FCSTD DOCUMENT  (FreeCAD 1.1R40444 (Git))
Label: Assembly
License: All rights reserved
LicenseURL: http://en.wikipedia.org/wiki/All_rights_reserved
objects: App::Link×5, App::FeaturePython×4, App::Point×1, Assembly::JointGroup×1, Assembly::AssemblyObject×1
EXTERNAL_REF file=Hull.FCStd obj=Body
EXTERNAL_REF file=Hull.FCStd obj=Sketch
EXTERNAL_REF file=Hull.FCStd obj=Body001
EXTERNAL_REF file=Gears.FCStd obj=Body001
EXTERNAL_REF file=Gears.FCStd obj=Body

FEATURE [App::Link] Hull
  LinkPlacement = pos=(0,0,0) rot=(0,1,0;0.032426rad)
  LinkedObject = -> <external Hull.FCStd>#Body
  Placement = pos=(0,0,0) rot=(0,1,0;0.032426rad)
FEATURE [App::FeaturePython] GroundedJoint  # Assembly grounded joint (typed FeaturePython)
  ObjectToGround = -> Hull
FEATURE [App::Link] Sketch
  LinkPlacement = pos=(-25.4586,-4.64916e-06,39) rot=(0,0,1;0rad)
  LinkedObject = -> <external Hull.FCStd>#Sketch
  Placement = pos=(-25.4586,-4.64916e-06,39) rot=(0,0,1;0rad)
FEATURE [App::Point] Origin001  label="Origin"
  Role = Origin
FEATURE [App::Link] Lid
  LinkPlacement = pos=(0.818028,-8.2e-14,22.9856) rot=(0,1,0;0.032426rad)
  LinkedObject = -> <external Hull.FCStd>#Body001
  Placement = pos=(0.818028,-8.2e-14,22.9856) rot=(0,1,0;0.032426rad)
FEATURE [App::FeaturePython] Joint  label="Fixed002"  # Assembly joint (typed FeaturePython)
  Activated = true
  AngleMax = 0
  AngleMin = 0
  Detach1 = false
  Detach2 = false
  Distance = 0
  Distance2 = 0
  EnableAngleMax = false
  EnableAngleMin = false
  EnableLengthMax = false
  EnableLengthMin = false
  JointType = 0 (Fixed)
  LengthMax = 0
  LengthMin = 0
  Placement1 = pos=(12.6239,8.51e-14,-1) rot=(0,0,1;0rad)
  Placement2 = pos=(12.6963,1.1e-15,22) rot=(0,0,1;0rad)
  Reference1 = -> Assembly [Lid.Pocket.Face7,Lid.Pocket.Face7]
  Reference2 = -> Assembly [Hull.Thickness.Face6,Hull.Thickness.Face6]
FEATURE [App::Link] SecondaryGear
  LinkPlacement = pos=(25.5722,1.157e-13,1.17155) rot=(0,1,0;0.032426rad)
  LinkedObject = -> <external Gears.FCStd>#Body001
  Placement = pos=(25.5722,1.157e-13,1.17155) rot=(0,1,0;0.032426rad)
FEATURE [App::FeaturePython] Joint001  label="Revolute006"  # Assembly joint (typed FeaturePython)
  Activated = true
  AngleMax = 0
  AngleMin = 0
  Detach1 = false
  Detach2 = false
  Distance = 0
  Distance2 = 0
  EnableAngleMax = false
  EnableAngleMin = false
  EnableLengthMax = false
  EnableLengthMin = false
  JointType = 1 (Revolute)
  LengthMax = 0
  LengthMin = 0
  Placement2 = pos=(25.5208,0,2) rot=(0,0,1;0rad)
  Reference1 = -> Assembly [SecondaryGear.Sketch003.Edge1,SecondaryGear.Sketch003.Edge1]
  Reference2 = -> Assembly [Hull.Face11,Hull.Edge3]
FEATURE [App::Link] MainGear
  LinkPlacement = pos=(-25.4515,-0.0167118,2.82664) rot=(0,1,0;0.032426rad)
  LinkedObject = -> <external Gears.FCStd>#Body
  Placement = pos=(-25.4515,-0.0167118,2.82664) rot=(0,1,0;0.032426rad)
FEATURE [App::FeaturePython] Joint002  label="Revolute008"  # Assembly joint (typed FeaturePython)
  Activated = true
  AngleMax = 0
  AngleMin = 0
  Detach1 = false
  Detach2 = false
  Distance = 0
  Distance2 = 0
  EnableAngleMax = false
  EnableAngleMin = false
  EnableLengthMax = false
  EnableLengthMin = false
  JointType = 1 (Revolute)
  LengthMax = 0
  LengthMin = 0
  Placement1 = pos=(0.00903,0.01671,0) rot=(0,0,1;0rad)
  Placement2 = pos=(-25.5208,0,2) rot=(0,0,1;0rad)
  Reference1 = -> Assembly [MainGear.Face241,MainGear.Edge104]
  Reference2 = -> Assembly [Hull.Face11,Hull.Edge1]
FEATURE [Assembly::JointGroup] Joints
  Group = -> [GroundedJoint,Joint,Joint001,Joint002]
FEATURE [Assembly::AssemblyObject] Assembly
  Group = -> [Joints,Hull,GroundedJoint,Sketch,Lid,Joint,SecondaryGear,Joint001,MainGear,Joint002]
  Origin = -> Origin
  Type = Assembly

RESOLVED EXTERNAL PARTS (link-assembly join: the EXTERNAL_REF files above that resolve inside this repo's crawl, each included once):
---- part Gears.FCStd = doc fcstd_c6806c5b29c4 ----
FCSTD DOCUMENT  (FreeCAD 1.1R40444 (Git))
Label: Gears
License: All rights reserved
LicenseURL: http://en.wikipedia.org/wiki/All_rights_reserved
objects: PartDesign::Pad×4, Sketcher::SketchObject×4, PartDesign::Body×3, App::Point×3, Part::Part2DObjectPython×2, PartDesign::ShapeBinder×2, PartDesign::Pocket×1
note: 30 computed .brp shape members not serialized (recipe doc carries the construction recipe); baked Part::Feature solids carry a one-line shape summary decoded from their .brp
EXTERNAL_REF file=Configuration.FCStd obj=Spreadsheet

FEATURE [Part::Part2DObjectPython] InvoluteGear  # Draft 2D object (typed FeaturePython)
  AddendumCoefficient = 1
  DedendumCoefficient = 1.25
  ExternalGear = true
  HighPrecision = true
  Modules = 1
  NumberOfTeeth = 24
  PressureAngle = 20
  ProfileShiftCoefficient = 0
  RootFilletCoefficient = 0.38
  expr: Modules = Configuration#Spreadsheet.gear_module
  expr: NumberOfTeeth = Configuration#<<Spreadsheet>>.main_gear_teeth
FEATURE [Part::Part2DObjectPython] InvoluteGear002  # Draft 2D object (typed FeaturePython)
  AddendumCoefficient = 1
  DedendumCoefficient = 1.25
  ExternalGear = true
  HighPrecision = true
  Modules = 1
  NumberOfTeeth = 48
  PressureAngle = 20
  ProfileShiftCoefficient = 0
  RootFilletCoefficient = 0.38
  expr: Modules = Configuration#Spreadsheet.gear_module
  expr: NumberOfTeeth = Configuration#Spreadsheet.secondary_gear_teeth
FEATURE [PartDesign::Pad] Pad
  Direction = (0,0,1)
  Length = 20
  Length2 = 10
  Profile = -> InvoluteGear
  ReferenceAxis = -> InvoluteGear [N_Axis]
  Refine = true
  Suppressed = false
  Type = 0
  expr: Length = <<Configuration>>#<<Spreadsheet>>.gear_height
FEATURE [PartDesign::Body] Body  label="MainGear"
  AllowCompound = false
  Group = -> [InvoluteGear,Pad]
  Origin = -> Origin
  Tip = -> Pad
FEATURE [PartDesign::Pad] Pad001
  Direction = (0,0,1)
  Length = 20
  Length2 = 10
  Profile = -> InvoluteGear002
  ReferenceAxis = -> InvoluteGear002 [N_Axis]
  Refine = true
  Suppressed = false
  Type = 0
  expr: Length = Configuration#<<Spreadsheet>>.gear_height
FEATURE [Sketcher::SketchObject] Sketch  label="ShaftMountInterface"
  ArcFitTolerance = 0
  ExternalTypes = [0]
  FullyConstrained = true
  MakeInternals = false
  expr: Constraints[26] = 1
  sketch-geometry (13):
    g0: LineSegment StartX=-4 StartY=-5 StartZ=0 EndX=4 EndY=-5 EndZ=0
    g1: LineSegment StartX=5 StartY=-4 StartZ=0 EndX=5 EndY=4 EndZ=0
    g2: LineSegment StartX=4 StartY=5 StartZ=0 EndX=-4 EndY=5 EndZ=0
    g3: LineSegment StartX=-5 StartY=4 StartZ=0 EndX=-5 EndY=-4 EndZ=0
    g4: GeomPoint [constr] X=0 Y=0 Z=0
    g5: ArcOfCircle CenterX=-4 CenterY=4 CenterZ=0 NormalX=0 NormalY=0 NormalZ=1 AngleXU=0 Radius=1 StartAngle=1.5708 EndAngle=3.14159
    g6: GeomPoint [constr] X=-5 Y=5 Z=0
    g7: ArcOfCircle CenterX=4 CenterY=4 CenterZ=0 NormalX=0 NormalY=0 NormalZ=1 AngleXU=0 Radius=1 StartAngle=0 EndAngle=1.5708
    g8: GeomPoint [constr] X=5 Y=5 Z=0
    g9: ArcOfCircle CenterX=4 CenterY=-4 CenterZ=0 NormalX=0 NormalY=0 NormalZ=1 AngleXU=0 Radius=1 StartAngle=4.71239 EndAngle=6.28319
    g10: GeomPoint [constr] X=5 Y=-5 Z=0
    g11: ArcOfCircle CenterX=-4 CenterY=-4 CenterZ=0 NormalX=0 NormalY=0 NormalZ=1 AngleXU=0 Radius=1 StartAngle=3.14159 EndAngle=4.71239
    g12: GeomPoint [constr] X=-5 Y=-5 Z=0
  constraints (28):
    c: Horizontal(g0)
    c: Horizontal(g2)
    c: Vertical(g1)
    c: Vertical(g3)
    c: Symmetric(g8,g12,g4)
    c: Coincident(g4,g-1)
    c: PointOnObject(g6,g2)
    c: PointOnObject(g6,g3)
    c: Tangent(g2,g5) = -1.5708
    c: Tangent(g3,g5) = -1.5708
    c: PointOnObject(g8,g1)
    c: PointOnObject(g8,g2)
    c: Tangent(g1,g7) = -1.5708
    c: Tangent(g2,g7) = -1.5708
    c: PointOnObject(g10,g0)
    c: PointOnObject(g10,g1)
    c: Tangent(g0,g9) = -1.5708
    c: Tangent(g1,g9) = -1.5708
    c: PointOnObject(g12,g0)
    c: PointOnObject(g12,g3)
    c: Tangent(g0,g11) = -1.5708
    c: Tangent(g3,g11) = -1.5708
    c: Distance(g4,g2) = 5
    c: Equal(g11,g5)
    c: Equal(g5,g7)
    c: Equal(g7,g9)
    c: Radius(g5) = 1
    c: Equal(g3,g2)
FEATURE [PartDesign::ShapeBinder] ShapeBinder
  Support = -> [Sketch]
  Suppressed = false
  TraceSupport = false
FEATURE [PartDesign::Pocket] Pocket
  BaseFeature = -> Pad001
  Direction = (0,0,-1)
  Length = 5
  Length2 = 5
  Profile = -> ShapeBinder
  Refine = true
  Reversed = true
  Suppressed = false
  Type = 1
FEATURE [PartDesign::ShapeBinder] ShapeBinder001
  Support = -> [Sketch]
  Suppressed = false
  TraceSupport = false
FEATURE [Sketcher::SketchObject] Sketch001
  ArcFitTolerance = 0
  AttachmentSupport = -> [Pocket]
  ExternalGeometry = -> [ShapeBinder001]
  ExternalTypes = [0]
  FullyConstrained = true
  MakeInternals = false
  MapMode = 5
  Placement = pos=(0,0,0) rot=(1,0,0;3.14159rad)
  sketch-geometry (15):
    g0: LineSegment StartX=4.8 StartY=-3.8 StartZ=0 EndX=4.8 EndY=3.8 EndZ=0
    g1: LineSegment StartX=3.8 StartY=4.8 StartZ=0 EndX=-3.8 EndY=4.8 EndZ=0
    g2: LineSegment StartX=-4.8 StartY=3.8 StartZ=0 EndX=-4.8 EndY=-3.8 EndZ=0
    g3: LineSegment StartX=-3.8 StartY=-4.8 StartZ=0 EndX=3.8 EndY=-4.8 EndZ=0
    g4: GeomPoint [constr] X=0 Y=0 Z=0
    g5: ArcOfCircle CenterX=-3.8 CenterY=3.8 CenterZ=0 NormalX=0 NormalY=0 NormalZ=1 AngleXU=0 Radius=1 StartAngle=1.5708 EndAngle=3.14159
    g6: GeomPoint [constr] X=-4.8 Y=4.8 Z=0
    g7: ArcOfCircle CenterX=3.8 CenterY=3.8 CenterZ=0 NormalX=0 NormalY=0 NormalZ=1 AngleXU=0 Radius=1 StartAngle=0 EndAngle=1.5708
    g8: GeomPoint [constr] X=4.8 Y=4.8 Z=0
    g9: ArcOfCircle CenterX=3.8 CenterY=-3.8 CenterZ=0 NormalX=0 NormalY=0 NormalZ=1 AngleXU=0 Radius=1 StartAngle=4.71239 EndAngle=6.28319
    g10: GeomPoint [constr] X=4.8 Y=-4.8 Z=0
    g11: ArcOfCircle CenterX=-3.8 CenterY=-3.8 CenterZ=0 NormalX=0 NormalY=0 NormalZ=1 AngleXU=0 Radius=1 StartAngle=3.14159 EndAngle=4.71239
    g12: GeomPoint [constr] X=-4.8 Y=-4.8 Z=0
    g13: LineSegment [constr] StartX=-5e-16 StartY=5 StartZ=0 EndX=1e-16 EndY=4.8 EndZ=0
    g14: LineSegment [constr] StartX=4.8 StartY=0 StartZ=0 EndX=5 EndY=2e-16 EndZ=0
  constraints (33):
    c: Vertical(g0)
    c: Vertical(g2)
    c: Horizontal(g1)
    c: Horizontal(g3)
    c: Symmetric(g6,g10,g4)
    c: Coincident(g4,g-1)
    c: PointOnObject(g6,g1)
    c: PointOnObject(g6,g2)
    c: Tangent(g1,g5) = -1.5708
    c: Tangent(g2,g5) = -1.5708
    c: PointOnObject(g8,g0)
    c: PointOnObject(g8,g1)
    c: Tangent(g0,g7) = -1.5708
    c: Tangent(g1,g7) = -1.5708
    c: PointOnObject(g10,g0)
    c: PointOnObject(g10,g3)
    c: Tangent(g0,g9) = -1.5708
    c: Tangent(g3,g9) = -1.5708
    c: PointOnObject(g12,g2)
    c: PointOnObject(g12,g3)
    c: Tangent(g2,g11) = -1.5708
    c: Tangent(g3,g11) = -1.5708
    c: Equal(g11,g-6)
    c: Equal(g5,g-4)
    c: Equal(g7,g-10)
    c: Equal(g1,g0)
    c: Distance(g-9,g0) = 0.2
    c: Symmetric(g-3,g-3,g13)
    c: Symmetric(g1,g1,g13)
    c: PointOnObject(g14,g-1)
    c: Symmetric(g-9,g-9,g14)
    c: Equal(g14,g13)
    c: PointOnObject(g14,g0)
FEATURE [PartDesign::Pad] Pad002
  Direction = (0,0,1)
  Length = 20
  Length2 = 10
  Profile = -> Sketch001
  ReferenceAxis = -> Sketch001 [N_Axis]
  Refine = true
  Suppressed = false
  Type = 0
  expr: Length = Configuration#Spreadsheet.gear_height
FEATURE [Sketcher::SketchObject] Sketch002
  ArcFitTolerance = 0
  AttachmentOffset = pos=(0,0,20) rot=(0,0,1;0rad)
  AttachmentSupport = -> [XY_Plane002]
  ExternalTypes = [0]
  FullyConstrained = true
  MakeInternals = false
  MapMode = 5
  Placement = pos=(0,0,20) rot=(0,0,1;0rad)
  expr: .AttachmentOffset.Base.z = Configuration#Spreadsheet.gear_height
  expr: Constraints[1] = Configuration#Spreadsheet.bearing_inner_diameter - 0.2
  sketch-geometry (1):
    g0: Circle CenterX=0 CenterY=0 CenterZ=0 NormalX=0 NormalY=0 NormalZ=1 AngleXU=0 Radius=3.9
  constraints (2):
    c: Coincident(g0,g-1)
    c: Diameter(g0) = 7.8
FEATURE [PartDesign::Pad] Pad003
  BaseFeature = -> Pad002
  Direction = (0,0,1)
  Length = 50
  Length2 = 10
  Profile = -> Sketch002
  ReferenceAxis = -> Sketch002 [N_Axis]
  Refine = true
  Suppressed = false
  Type = 0
FEATURE [PartDesign::Body] Body002  label="Shaft"
  AllowCompound = false
  Group = -> [ShapeBinder001,Sketch001,Pad002,Sketch002,Pad003]
  Origin = -> Origin002
  Tip = -> Pad003
FEATURE [App::Point] Origin003  label="Origin"
  Role = Origin
FEATURE [App::Point] Origin004  label="Origin"
  Role = Origin
FEATURE [App::Point] Origin005  label="Origin"
  Role = Origin
FEATURE [Sketcher::SketchObject] Sketch003
  ArcFitTolerance = 1e-06
  ExternalGeometry = -> [Pocket]
  ExternalTypes = [0,0]
  FullyConstrained = true
  MakeInternals = false
  sketch-geometry (1):
    g0: Circle CenterX=0 CenterY=0 CenterZ=0 NormalX=0 NormalY=0 NormalZ=1 AngleXU=0 Radius=25.0003
  constraints (2):
    c: Coincident(g0,g-1)
    c: PointOnObject(g-3,g0)
FEATURE [PartDesign::Body] Body001  label="SecondaryGear"
  AllowCompound = false
  Group = -> [InvoluteGear002,Pad001,ShapeBinder,Pocket,Sketch003]
  Origin = -> Origin001
  Tip = -> Pocket
---- part Hull.FCStd = doc fcstd_253122ee288d ----
FCSTD DOCUMENT  (FreeCAD 1.1R40444 (Git))
Label: Hull
License: All rights reserved
LicenseURL: http://en.wikipedia.org/wiki/All_rights_reserved
objects: PartDesign::ShapeBinder×4, PartDesign::Pad×3, Sketcher::SketchObject×2, App::Point×2, PartDesign::Body×2, PartDesign::Pocket×1, PartDesign::Thickness×1
note: 25 computed .brp shape members not serialized (recipe doc carries the construction recipe); baked Part::Feature solids carry a one-line shape summary decoded from their .brp
EXTERNAL_REF file=Configuration.FCStd obj=Spreadsheet

FEATURE [Sketcher::SketchObject] Sketch
  ArcFitTolerance = 0
  AttachmentSupport = -> [XY_Plane]
  ExternalTypes = [0]
  FullyConstrained = false
  MakeInternals = false
  MapMode = 5
  expr: Constraints[4] = 35 mm
  sketch-geometry (4):
    g0: ArcOfCircle CenterX=-25.5208 CenterY=0 CenterZ=0 NormalX=0 NormalY=0 NormalZ=1 AngleXU=0 Radius=16 StartAngle=1.95222 EndAngle=4.33096
    g1: ArcOfCircle CenterX=25.5208 CenterY=0 CenterZ=0 NormalX=0 NormalY=0 NormalZ=1 AngleXU=0 Radius=35 StartAngle=4.33096 EndAngle=8.23541
    g2: LineSegment StartX=-31.4767 StartY=14.8501 StartZ=0 EndX=12.4922 EndY=32.4847 EndZ=0
    g3: LineSegment StartX=-31.4767 StartY=-14.8501 StartZ=0 EndX=12.4922 EndY=-32.4847 EndZ=0
  constraints (8):
    c: Tangent(g0,g2) = 1.5708
    c: Tangent(g0,g3) = -1.5708
    c: Tangent(g1,g2) = 1.5708
    c: Tangent(g1,g3) = -1.5708
    c: Radius(g1) = 35
    c: PointOnObject(g0,g-1)
    c: Symmetric(g0,g1,g-2)
    c: Radius(g0) = 16
FEATURE [PartDesign::ShapeBinder] ShapeBinder
  Support = -> [Sketch]
  Suppressed = false
  TraceSupport = false
FEATURE [PartDesign::Pad] Pad
  Direction = (0,0,1)
  Length = 22
  Length2 = 10
  Profile = -> ShapeBinder
  Refine = true
  Suppressed = false
  Type = 0
  expr: Length = Configuration#Spreadsheet.gear_height + 2
FEATURE [PartDesign::ShapeBinder] ShapeBinder001
  Support = -> [Sketch]
  Suppressed = false
  TraceSupport = false
FEATURE [Sketcher::SketchObject] Sketch001
  ArcFitTolerance = 0
  AttachmentSupport = -> [XY_Plane001]
  ExternalGeometry = -> [ShapeBinder001]
  ExternalTypes = [1]
  FullyConstrained = true
  MakeInternals = false
  MapMode = 5
  sketch-geometry (1):
    g0: Circle CenterX=25.5208 CenterY=0 CenterZ=0 NormalX=0 NormalY=0 NormalZ=1 AngleXU=0 Radius=10
  constraints (2):
    c: Diameter(g0) = 20
    c: Coincident(g-3,g0)
FEATURE [PartDesign::ShapeBinder] ShapeBinder002
  Support = -> [Sketch001]
  Suppressed = false
  TraceSupport = false
FEATURE [PartDesign::Pad] Pad001
  Direction = (0,0,1)
  Length = 2
  Length2 = 10
  Profile = -> ShapeBinder002
  Refine = true
  Suppressed = false
  Type = 0
FEATURE [PartDesign::ShapeBinder] ShapeBinder003
  Support = -> [Sketch001]
  Suppressed = false
  TraceSupport = false
FEATURE [PartDesign::Pad] Pad002
  BaseFeature = -> Pad001
  Direction = (0,0,1)
  Length = 1
  Length2 = 10
  Profile = -> ShapeBinder003
  Refine = true
  Reversed = true
  Suppressed = false
  Type = 0
FEATURE [App::Point] Origin002  label="Origin"
  Role = Origin
FEATURE [App::Point] Origin003  label="Origin"
  Role = Origin
FEATURE [PartDesign::Pocket] Pocket
  BaseFeature = -> Pad002
  Direction = (0,0,-1)
  Length = 5
  Length2 = 5
  Profile = -> Sketch001
  ReferenceAxis = -> Sketch001 [N_Axis]
  Refine = true
  Reversed = true
  Suppressed = false
  Type = 1
FEATURE [PartDesign::Body] Body001  label="Lid"
  AllowCompound = false
  Group = -> [ShapeBinder001,Sketch001,ShapeBinder002,Pad001,ShapeBinder003,Pad002,Pocket]
  Origin = -> Origin001
  Tip = -> Pocket
FEATURE [PartDesign::Thickness] Thickness
  Base = -> Pad [Face6]
  BaseFeature = -> Pad
  Intersection = false
  Join = 0
  Mode = 0
  Refine = true
  Reversed = true
  SupportTransform = false
  Suppressed = false
  Value = 2
  expr: Value = 2
FEATURE [PartDesign::Body] Body  label="Hull"
  AllowCompound = false
  Group = -> [ShapeBinder,Pad,Thickness]
  Origin = -> Origin
  Tip = -> Thickness
